# Revit family: Pipe-Strap-Atkore-Single-Piece-P2558-60
name_source: partatom
category: Specialty Equipment
revit_build: Autodesk Revit MEP 2012 (Build: 20110309_2315(x64)
units: mm (PartAtom-declared; Revit-internal decimal feet)

## types (1)
- P2558-60
    04 CSI = 26 05 48
    95 CSI = 16070
    Assembly Code = D5090300
    Conduit Size = 9.5 mm  [stored 0.031168 ft]
    Description = Single Piece Pipe Strap
    Load Capacity Note = Visit the product page for load application and capacity.
    Manufacturer = Unistrut by Atkore International
    Manufacturer Fax = 708-339-7814
    Material = Multiple Options - See Catalog
    Model = P2558-60
    Overall Depth = 41.27 mm
    Overall Height = 173.75 mm
    Overall Width = 253.25 mm
    Part Number = P2558-60
    Part Type = Strap
    Subcategory = Pipe Strap
    Thickness = 3.2 mm  [stored 0.0104987 ft]
    URL = http://unistrut.us
    Unit = Metal - Aluminum - Atkore - Electro - Galvanized

note: [stored X ft] marks values corroborated as IEEE doubles in the binary element streams (Revit-internal decimal feet)

## geometry (parser evidence)
native form markers: Blend x4, Sweep x4
no freeform markers — native parametric forms only
